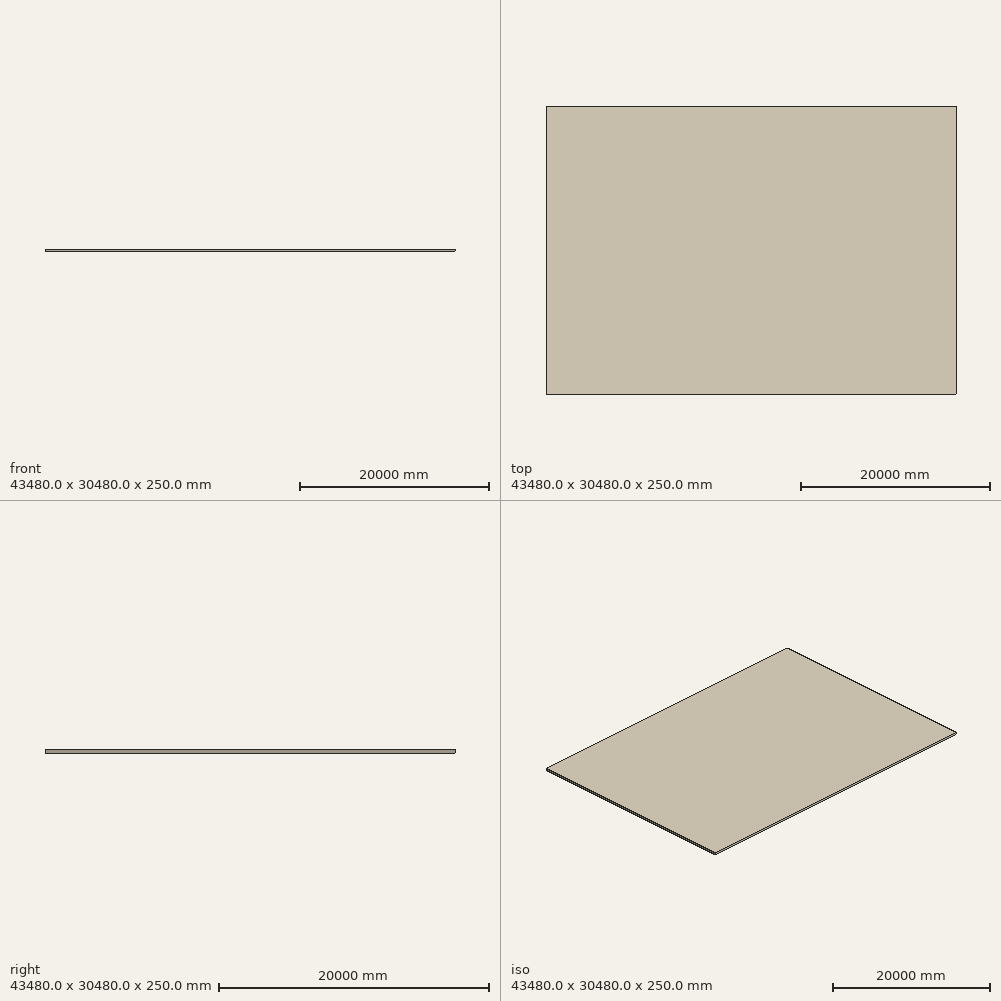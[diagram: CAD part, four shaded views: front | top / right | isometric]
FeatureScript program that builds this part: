
annotation { "Feature Type Name" : "Feature", "Feature Type Description" : "" }
export const myFeature = defineFeature(function(context is Context, id is Id, definition is map)
    precondition{}
    {
        {
            var Q0;
            Q0=qCreatedBy(makeId("Top.planeOp"),FACE);
            var sketch = newSketch(context, id + "F0", { "sketchPlane" : qUnion([Q0])});
            skLineSegment(sketch, "E0.bottom", {"start": v(-21740, 15240) * mm, "end": v(21740, 15240) * mm});
            skLineSegment(sketch, "E0.top", {"start": v(-21740, -15240) * mm, "end": v(21740, -15240) * mm});
            skLineSegment(sketch, "E0.left", {"start": v(-21740, 15240) * mm, "end": v(-21740, -15240) * mm});
            skLineSegment(sketch, "E0.right", {"start": v(21740, 15240) * mm, "end": v(21740, -15240) * mm});
            skPoint(sketch, "E0.middle", {"position": v(0, 0) * mm});
            skSolve(sketch);
        }
        {
            var Q0;
            Q0 = qSketchRegion(id + "F0", true);
            var Q1;
            Q1=makeQuery(id+"F0.imprint","IMPRINT",FACE,{"disambiguationData":[TD([[makeQuery(id+"F0.imprint","IMPRINT",EDGE,{"derivedFrom":sQuery(id+"F0.wireOp",EDGE,"E0.bottom")}),-1.0]])]});
            extrude(context, id + "F1", {"entities" : qUnion([Q0, Q1]), "depth" : 250 * mm});
        }
    });
